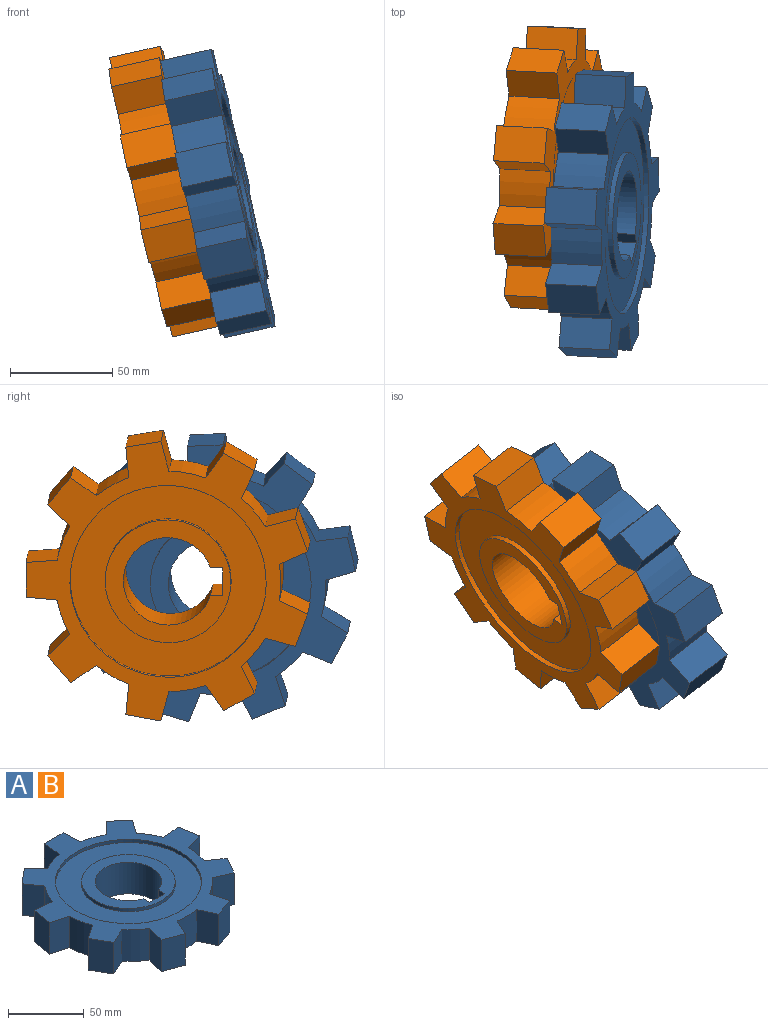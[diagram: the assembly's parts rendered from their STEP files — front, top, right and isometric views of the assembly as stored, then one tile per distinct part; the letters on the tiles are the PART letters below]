
ASSEMBLY  parts=2 mates=1
PART A: 50 faces, bbox 140x137.9x25.4 mm
  f0: plane 61.53x61.53mm, normal (0,0,1), area 1394mm2, adj f40,f44,f47,f48,f49
  f1: plane 61.53x61.53mm, normal (0,0,-1), area 1394mm2, adj f40,f41,f47,f48,f49
  f2: plane 25.4x15.22mm, normal (0.09,1,0), area 388.1mm2, adj f3,f37,f38,f39
  f3: plane 25.4x17.16mm, normal (-0.98,0.17,0), area 442.6mm2, adj f2,f4,f38,f39
  f4: plane 25.4x14.77mm, normal (-0.26,-0.97,0), area 388.1mm2, adj f3,f5,f38,f39
  f5: cylinder r=55.24mm len=25.4mm, axis (0,0,-1), area 468.2mm2, adj f4,f6,f38,f39
  f6: plane 25.4x12.54mm, normal (-0.57,0.82,0), area 388.1mm2, adj f5,f7,f38,f39
  f7: plane 25.4x15.09mm, normal (-0.87,-0.5,0), area 442.6mm2, adj f6,f8,f38,f39
  f8: plane 25.4x13.83mm, normal (0.42,-0.91,0), area 388.1mm2, adj f7,f9,f38,f39
  f9: cylinder r=55.24mm len=25.4mm, axis (0,0,-1), area 468.2mm2, adj f8,f10,f38,f39
  f10: plane 25.4x14.75mm, normal (-0.97,0.26,0), area 388.1mm2, adj f9,f11,f38,f39
  f11: plane 25.4x16.37mm, normal (-0.34,-0.94,0), area 442.6mm2, adj f10,f12,f38,f39
  f12: plane 25.4x13.86mm, normal (0.91,-0.42,0), area 388.1mm2, adj f11,f13,f38,f39
  f13: cylinder r=55.24mm len=25.4mm, axis (0,0,-1), area 468.2mm2, adj f12,f14,f38,f39
  f14: plane 25.4x13.86mm, normal (-0.91,-0.42,0), area 388.1mm2, adj f13,f15,f38,f39
  f15: plane 25.4x16.37mm, normal (0.34,-0.94,0), area 442.6mm2, adj f14,f16,f38,f39
  f16: plane 25.4x14.75mm, normal (0.97,0.26,0), area 388.1mm2, adj f15,f17,f38,f39
  f17: cylinder r=55.24mm len=25.4mm, axis (0,0,-1), area 468.2mm2, adj f16,f18,f38,f39
  f18: plane 25.4x13.83mm, normal (-0.42,-0.91,0), area 388.1mm2, adj f17,f19,f38,f39
  f19: plane 25.4x15.09mm, normal (0.87,-0.5,0), area 442.6mm2, adj f18,f20,f38,f39
  f20: plane 25.4x12.54mm, normal (0.57,0.82,0), area 388.1mm2, adj f19,f21,f38,f39
  f21: cylinder r=55.24mm len=25.4mm, axis (0,0,-1), area 468.2mm2, adj f20,f22,f38,f39
  f22: plane 25.4x14.77mm, normal (0.26,-0.97,0), area 388.1mm2, adj f21,f23,f38,f39
  f23: plane 25.4x17.16mm, normal (0.98,0.17,0), area 442.6mm2, adj f22,f24,f38,f39
  f24: plane 25.4x15.22mm, normal (-0.09,1,0), area 388.1mm2, adj f23,f25,f38,f39
  f25: cylinder r=55.24mm len=25.4mm, axis (0,0,-1), area 468.2mm2, adj f24,f26,f38,f39
  f26: plane 25.4x12.5mm, normal (0.82,-0.58,0), area 388.1mm2, adj f25,f27,f38,f39
  f27: plane 25.4x13.35mm, normal (0.64,0.77,0), area 442.6mm2, adj f26,f28,f38,f39
  f28: plane 25.4x10.83mm, normal (-0.71,0.71,0), area 388.1mm2, adj f27,f29,f38,f39
  f29: cylinder r=55.24mm len=25.4mm, axis (0,0,-1), area 468.2mm2, adj f28,f30,f38,f39
  f30: plane 25.4x15.23mm, normal (1,0.08,0), area 388.1mm2, adj f29,f31,f38,f39
  f31: plane 25.4x17.42mm, normal (0,1,0), area 442.6mm2, adj f30,f32,f38,f39
  f32: plane 25.4x15.23mm, normal (-1,0.08,0), area 388.1mm2, adj f31,f33,f38,f39
  f33: cylinder r=55.24mm len=25.4mm, axis (0,0,-1), area 468.2mm2, adj f32,f34,f38,f39
  f34: plane 25.4x10.83mm, normal (0.71,0.71,0), area 388.1mm2, adj f33,f35,f38,f39
  f35: plane 25.4x13.35mm, normal (-0.64,0.77,0), area 442.6mm2, adj f34,f36,f38,f39
  f36: plane 25.4x12.5mm, normal (-0.82,-0.58,0), area 388.1mm2, adj f35,f37,f38,f39
  f37: cylinder r=55.24mm len=25.4mm, axis (0,0,-1), area 468.2mm2, adj f2,f36,f38,f39
  f38: plane 140.01x137.88mm, normal (0,0,1), area 4786.7mm2, adj f2,f3,f4,f5,f6,f7,f8,f9
  f39: plane 140.01x137.88mm, normal (0,0,-1), area 4786.7mm2, adj f2,f3,f4,f5,f6,f7,f8,f9
  f40: cylinder r=21.91mm len=43.81mm, axis (0,0,-1), area 3135.2mm2, adj f0,f1,f48,f49
  f41: cylinder r=30.77mm len=61.53mm, axis (0,0,-1), area 491mm2, adj f1,f43
  f42: cylinder r=48.05mm len=96.1mm, axis (0,0,-1), area 766.8mm2, adj f39,f43
  f43: plane 96.1x96.1mm, normal (0,0,-1), area 4279.6mm2, adj f41,f42
  f44: cylinder r=30.77mm len=61.53mm, axis (0,0,1), area 491mm2, adj f0,f46
  f45: cylinder r=48.05mm len=96.1mm, axis (0,0,1), area 766.8mm2, adj f38,f46
  f46: plane 96.1x96.1mm, normal (0,0,1), area 4279.6mm2, adj f44,f45
  f47: plane 25.4x13.94mm, normal (0,1,0), area 354.1mm2, adj f0,f1,f48,f49
  f48: plane 25.4x5.93mm, normal (-1,0,0), area 150.6mm2, adj f0,f1,f40,f47
  f49: plane 25.4x5.97mm, normal (1,0,0), area 151.7mm2, adj f0,f1,f40,f47
PART B: same geometry as A
PLACE A rot(axis=(0.38,0.82,0.43),87.5deg) t=(115.48,-11.37,61.48)mm
PLACE B rot(axis=(0.03,1,-0.02),77.4deg) t=(90.21,10.64,62.88)mm
MATE revolute A.f40 <-> B.f0  axis (-0.97,0.05,-0.22) through (115.48,-11.37,61.48)mm
